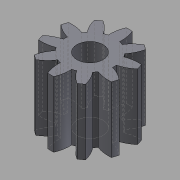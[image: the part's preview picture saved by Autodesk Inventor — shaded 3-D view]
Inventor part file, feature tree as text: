
AUTODESK INVENTOR PART (.ipt)
format: ipt  version: 2015 (Build 190159000, 159)  size: 164,352 bytes
history: native  units: in
note: dims shown in document units (in); Inventor stores cm internally (conversion verified against a paired STEP export)
features: other x13, sketch x3, plane x2
ambient origin geometry x8: Origin, YZ Plane, XZ Plane, XY Plane, X Axis, Y Axis, Z Axis, Center Point
bodies: Solid1 (feature_tree)
feature tree (18):
  other  "Spur Gear1"
  other  "Solid1::Spur Gear1"
  other  "TaggingFeature1"
  sketch  "Sketch1"  dims[d0=0.3937in]
  sketch  "Sketch2"  dims[d16=0.4724in d17=0.0in d41=0.0in d43=0.4724in d46=0.4724in d47=0.0in d48=0.0in]
  sketch  "Sketch3"
  plane  "XZ Plane_1"
  plane  "Work Plane2"
  other  "Z Axis_1"
  other  "Srf1"
  other  "Srf1::Derived"
  other  "Distance iMate"
  other  "Align iMate"
  other  "Mesh iMate"
  other  "Axis iMate"
  other  "Position iMate"
  other  "Mesh iMate2"
  other  "Start plane iMate"
